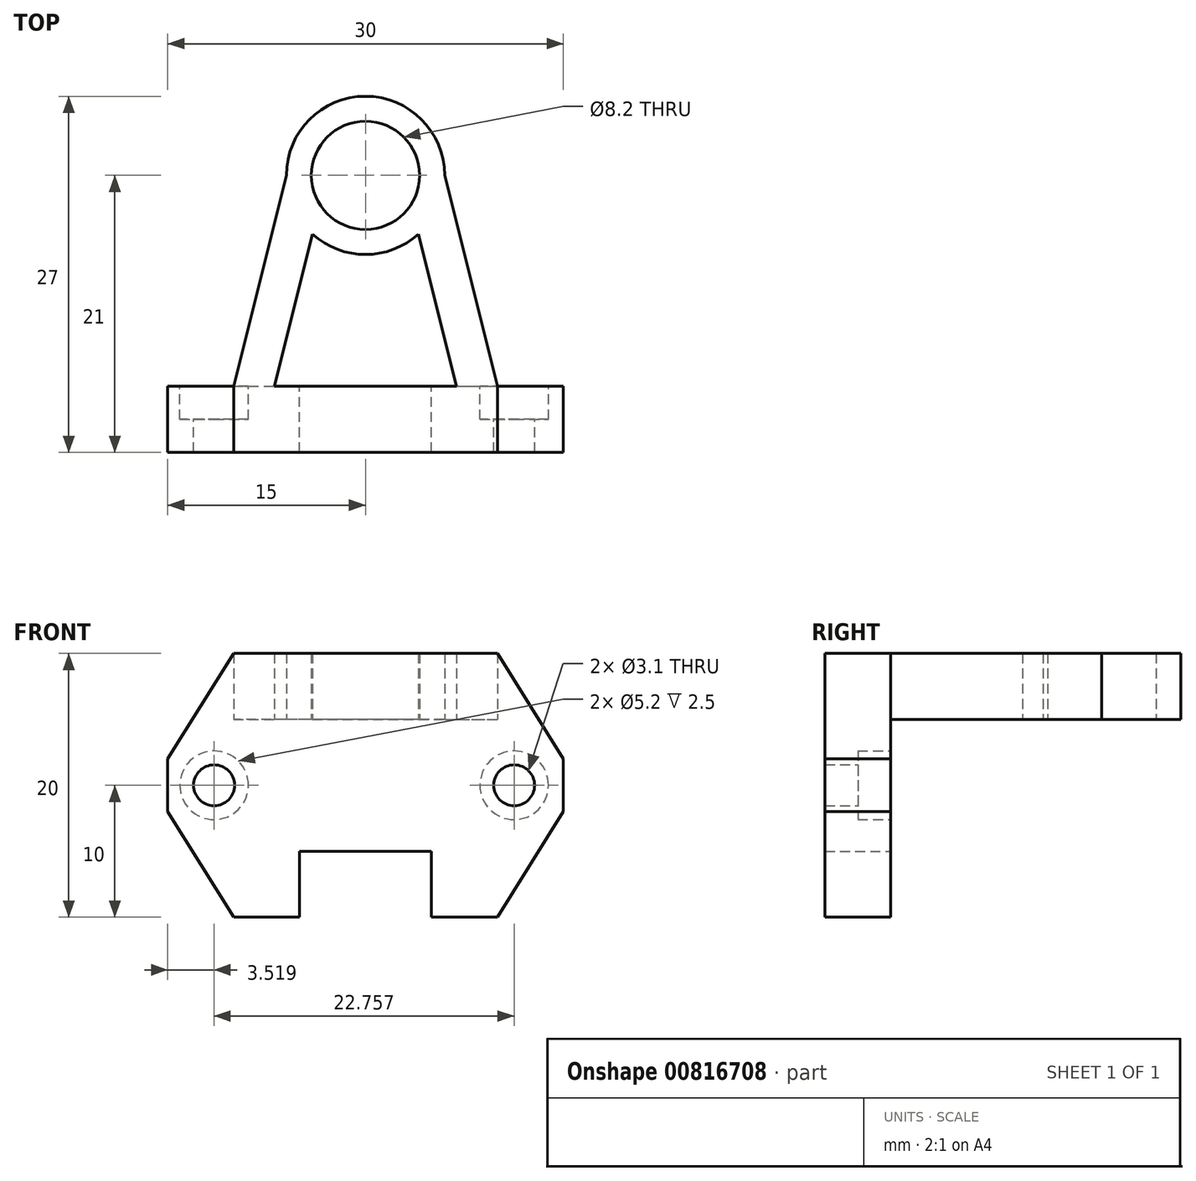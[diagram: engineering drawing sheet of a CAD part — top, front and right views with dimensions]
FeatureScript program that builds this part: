
annotation { "Feature Type Name" : "Feature", "Feature Type Description" : "" }
export const myFeature = defineFeature(function(context is Context, id is Id, definition is map)
    precondition{}
    {
        {
            var Q0;
            Q0=qCreatedBy(makeId("Top.planeOp"),FACE);
            var sketch = newSketch(context, id + "F0", { "sketchPlane" : qUnion([Q0])});
            skLineSegment(sketch, "E0.bottom", {"start": v(0, 0) * mm, "end": v(30, 0) * mm});
            skLineSegment(sketch, "E0.top", {"start": v(0, 5) * mm, "end": v(5, 5) * mm});
            skLineSegment(sketch, "E0.left", {"start": v(0, 0) * mm, "end": v(0, 5) * mm});
            skLineSegment(sketch, "E0.right", {"start": v(30, 0) * mm, "end": v(30, 5) * mm});
            skCircle(sketch, "E1", {"center": v(15, 21) * mm, "radius": 4.1 * mm});
            skArc(sketch, "E2", {"start": v(10.98, 16.55) * mm, "mid": v(15, 15) * mm, "end": v(19.02, 16.55) * mm});
            skLineSegment(sketch, "E3", {"start": v(21, 21) * mm, "end": v(25, 5) * mm});
            skLineSegment(sketch, "E4", {"start": v(9, 21) * mm, "end": v(5, 5) * mm});
            skLineSegment(sketch, "E5.0", {"start": v(10.98, 16.55) * mm, "end": v(8.1, 5) * mm});
            skLineSegment(sketch, "E6.trimOffspring", {"start": v(19.02, 16.55) * mm, "end": v(21.9, 5) * mm});
            skArc(sketch, "E7.trimOffspring", {"start": v(21, 21) * mm, "mid": v(15, 27) * mm, "end": v(9, 21) * mm});
            skLineSegment(sketch, "E8.trimOffspring", {"start": v(8.1, 5) * mm, "end": v(21.9, 5) * mm});
            skLineSegment(sketch, "E9.trimOffspring", {"start": v(25, 5) * mm, "end": v(30, 5) * mm});
            skSolve(sketch);
        }
        {
            var Q0;
            Q0 = qSketchRegion(id + "F0", true);
            extrude(context, id + "F1", {"entities" : qUnion([Q0]), "depth" : 5 * mm, "offsetDistance" : 25 * mm});
        }
        {
            var Q0;
            Q0=makeQuery(id+"F1.opExtrude","SWEPT_FACE",FACE,{"disambiguationData":[OSD([sQuery(id+"F0.wireOp",EDGE,"E0.bottom")])]});
            var sketch = newSketch(context, id + "F2", { "sketchPlane" : qUnion([Q0])});
            skLineSegment(sketch, "E10.bottom", {"start": v(0, -15) * mm, "end": v(30, -15) * mm});
            skLineSegment(sketch, "E10.top", {"start": v(0, 5) * mm, "end": v(30, 5) * mm});
            skLineSegment(sketch, "E10.left", {"start": v(0, -15) * mm, "end": v(0, 5) * mm});
            skLineSegment(sketch, "E10.right", {"start": v(30, -15) * mm, "end": v(30, 5) * mm});
            skSolve(sketch);
        }
        {
            var Q0;
            Q0 = qSketchRegion(id + "F2", true);
            extrude(context, id + "F3", {"entities" : qUnion([Q0]), "operationType" : NewBodyOperationType.ADD, "oppositeDirection" : true, "depth" : 5 * mm, "offsetDistance" : 25 * mm});
        }
        {
            var Q0;
            Q0=makeQuery(id+"F3.boolean.opBoolean","MERGE",FACE,{"derivedFrom":[makeQuery(id+"F1.opExtrude","SWEPT_FACE",FACE,{"disambiguationData":[OSD([sQuery(id+"F0.wireOp",EDGE,"E0.top")])]}),makeQuery(id+"F1.opExtrude","SWEPT_FACE",FACE,{"disambiguationData":[OSD([sQuery(id+"F0.wireOp",EDGE,"E8.trimOffspring")])]}),makeQuery(id+"F1.opExtrude","SWEPT_FACE",FACE,{"disambiguationData":[OSD([sQuery(id+"F0.wireOp",EDGE,"E9.trimOffspring")])]}),makeQuery(id+"F3.opExtrude","CAP_FACE",FACE,{"disambiguationData":[OSD([sQuery(id+"F2.wireOp",EDGE,"E10.bottom"),sQuery(id+"F2.wireOp",EDGE,"E10.top"),sQuery(id+"F2.wireOp",EDGE,"E10.left"),sQuery(id+"F2.wireOp",EDGE,"E10.right")])],"isStart":false})]});
            var sketch = newSketch(context, id + "F4", { "sketchPlane" : qUnion([Q0])});
            skCircle(sketch, "E11", {"center": v(-26.28, -5) * mm, "radius": 1.55 * mm});
            skCircle(sketch, "E12", {"center": v(-3.52, -5) * mm, "radius": 1.55 * mm});
            skLineSegment(sketch, "E13", {"start": v(-25, 5) * mm, "end": v(-30, -3) * mm});
            skLineSegment(sketch, "E14", {"start": v(-30, -3) * mm, "end": v(-30, 5) * mm});
            skLineSegment(sketch, "E15", {"start": v(-30, 5) * mm, "end": v(-25, 5) * mm});
            skLineSegment(sketch, "E16", {"start": v(0, 5) * mm, "end": v(-5, 5) * mm});
            skLineSegment(sketch, "E17", {"start": v(-5, 5) * mm, "end": v(0, -3) * mm});
            skLineSegment(sketch, "E18", {"start": v(0, -3) * mm, "end": v(0, 5) * mm});
            skLineSegment(sketch, "E19", {"start": v(-25, -15) * mm, "end": v(-30, -7) * mm});
            skLineSegment(sketch, "E20", {"start": v(-30, -7) * mm, "end": v(-30, -15) * mm});
            skLineSegment(sketch, "E21", {"start": v(-30, -15) * mm, "end": v(-25, -15) * mm});
            skLineSegment(sketch, "E22", {"start": v(0, -15) * mm, "end": v(-5, -15) * mm});
            skLineSegment(sketch, "E23", {"start": v(-5, -15) * mm, "end": v(0, -7) * mm});
            skLineSegment(sketch, "E24", {"start": v(0, -7) * mm, "end": v(0, -15) * mm});
            skLineSegment(sketch, "E25.bottom", {"start": v(-20, -15) * mm, "end": v(-10, -15) * mm});
            skLineSegment(sketch, "E25.top", {"start": v(-20, -10) * mm, "end": v(-10, -10) * mm});
            skLineSegment(sketch, "E25.left", {"start": v(-20, -15) * mm, "end": v(-20, -10) * mm});
            skLineSegment(sketch, "E25.right", {"start": v(-10, -15) * mm, "end": v(-10, -10) * mm});
            skSolve(sketch);
        }
        {
            var Q0;
            Q0 = qSketchRegion(id + "F4", true);
            extrude(context, id + "F5", {"entities" : qUnion([Q0]), "operationType" : NewBodyOperationType.REMOVE, "oppositeDirection" : true, "depth" : 5 * mm, "offsetDistance" : 25 * mm});
        }
        {
            var Q0;
            Q0=makeQuery(id+"F3.boolean.opBoolean","MERGE",FACE,{"derivedFrom":[makeQuery(id+"F1.opExtrude","SWEPT_FACE",FACE,{"disambiguationData":[OSD([sQuery(id+"F0.wireOp",EDGE,"E0.top")])]}),makeQuery(id+"F1.opExtrude","SWEPT_FACE",FACE,{"disambiguationData":[OSD([sQuery(id+"F0.wireOp",EDGE,"E8.trimOffspring")])]}),makeQuery(id+"F1.opExtrude","SWEPT_FACE",FACE,{"disambiguationData":[OSD([sQuery(id+"F0.wireOp",EDGE,"E9.trimOffspring")])]}),makeQuery(id+"F3.opExtrude","CAP_FACE",FACE,{"disambiguationData":[OSD([sQuery(id+"F2.wireOp",EDGE,"E10.bottom"),sQuery(id+"F2.wireOp",EDGE,"E10.top"),sQuery(id+"F2.wireOp",EDGE,"E10.left"),sQuery(id+"F2.wireOp",EDGE,"E10.right")])],"isStart":false})]});
            var sketch = newSketch(context, id + "F6", { "sketchPlane" : qUnion([Q0])});
            skCircle(sketch, "E26", {"center": v(-26.28, -5) * mm, "radius": 2.6 * mm});
            skCircle(sketch, "E27", {"center": v(-3.52, -5) * mm, "radius": 2.6 * mm});
            skSolve(sketch);
        }
        {
            var Q0;
            Q0 = qSketchRegion(id + "F6", true);
            extrude(context, id + "F7", {"entities" : qUnion([Q0]), "operationType" : NewBodyOperationType.REMOVE, "oppositeDirection" : true, "depth" : 2.5 * mm, "offsetDistance" : 25 * mm});
        }
    });
